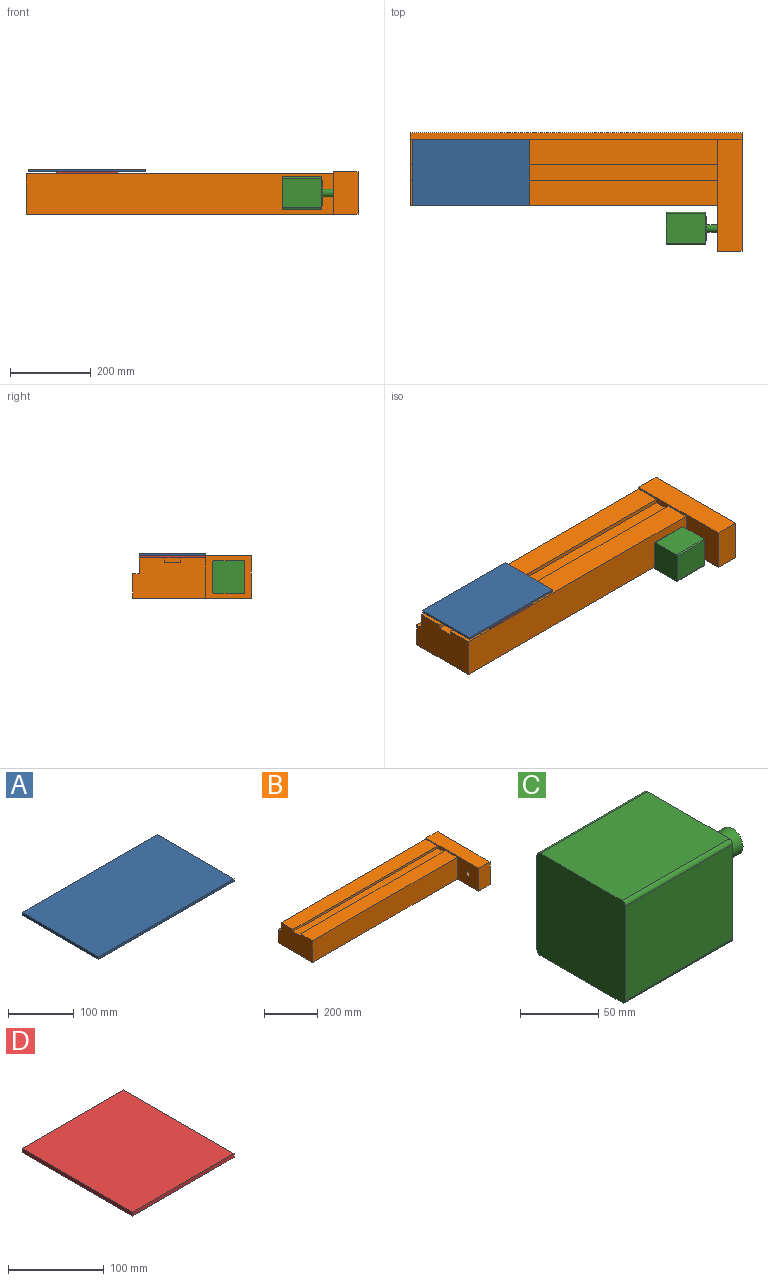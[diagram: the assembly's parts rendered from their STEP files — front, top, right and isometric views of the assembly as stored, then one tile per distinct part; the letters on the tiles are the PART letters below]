
ASSEMBLY  parts=4 mates=3
PART A: 6 faces, bbox 290x165x5 mm
  f0: plane 165x5mm, normal (-1,0,0), area 825mm2, adj f1,f3,f4,f5
  f1: plane 290x5mm, normal (0,-1,0), area 1450mm2, adj f0,f2,f4,f5
  f2: plane 165x5mm, normal (1,0,0), area 825mm2, adj f1,f3,f4,f5
  f3: plane 290x5mm, normal (0,1,0), area 1450mm2, adj f0,f2,f4,f5
  f4: plane 290x165mm, normal (0,0,1), area 47850mm2, adj f0,f1,f2,f3
  f5: plane 290x165mm, normal (0,0,-1), area 47850mm2, adj f0,f1,f2,f3
PART B: 17 faces, bbox 820x293x104 mm
  f0: plane 760x62.5mm, normal (0,0,1), area 47500mm2, adj f1,f6,f10,f12
  f1: plane 181x99mm, normal (-1,0,0), area 16895mm2, adj f0,f2,f3,f4,f5,f6,f11,f12
  f2: plane 760x99mm, normal (0,-1,0), area 75240mm2, adj f1,f3,f10,f11
  f3: plane 820x293mm, normal (0,0,-1), area 155140mm2, adj f1,f2,f4,f8,f9,f10
  f4: plane 820x60mm, normal (0,1,0), area 49200mm2, adj f1,f3,f5,f8
  f5: plane 820x16mm, normal (0,0,1), area 13120mm2, adj f1,f4,f6,f8
  f6: plane 820x44mm, normal (0,1,0), area 32280mm2, adj f0,f1,f5,f7,f8,f10
  f7: plane 277x60mm, normal (0,0,1), area 16620mm2, adj f6,f8,f9,f10
  f8: plane 293x104mm, normal (1,0,0), area 29768mm2, adj f3,f4,f5,f6,f7,f9
  f9: plane 104x60mm, normal (0,-1,0), area 6240mm2, adj f3,f7,f8,f10
  f10: plane 277x104mm, normal (-1,0,0), area 12558.8mm2, adj f0,f2,f3,f6,f7,f9,f11,f12
  f11: plane 760x62.5mm, normal (0,0,1), area 47500mm2, adj f1,f2,f10,f13
  f12: plane 760x10mm, normal (0,-1,0), area 7600mm2, adj f0,f1,f10,f14
  f13: plane 760x10mm, normal (0,1,0), area 7600mm2, adj f1,f10,f11,f14
  f14: plane 760x40mm, normal (0,0,1), area 30400mm2, adj f1,f10,f12,f13
  f15: cylinder r=10mm len=20mm, axis (-1,0,0), area 1256.6mm2, adj f10,f16
  f16: plane 20x20mm, normal (-1,0,0), area 314.2mm2, adj f15
PART C: 14 faces, bbox 137x80x80 mm
  f0: plane 97x74mm, normal (0,0,1), area 7178mm2, adj f4,f5,f10,f13
  f1: plane 97x74mm, normal (0,-1,0), area 7178mm2, adj f4,f5,f10,f11
  f2: plane 97x74mm, normal (0,0,-1), area 7178mm2, adj f4,f5,f11,f12
  f3: plane 97x74mm, normal (0,1,0), area 7178mm2, adj f4,f5,f12,f13
  f4: plane 80x80mm, normal (1,0,0), area 3564.8mm2, adj f0,f1,f2,f3,f6,f10,f11,f12
  f5: plane 80x80mm, normal (-1,0,0), area 6392.3mm2, adj f0,f1,f2,f3,f10,f11,f12,f13
  f6: cylinder r=30mm len=60mm, axis (-1,0,0), area 565.5mm2, adj f4,f7
  f7: plane 60x60mm, normal (1,0,0), area 2543.9mm2, adj f6,f9
  f8: plane 19x19mm, normal (1,0,0), area 283.5mm2, adj f9
  f9: cylinder r=9.5mm len=37mm, axis (-1,0,0), area 2208.5mm2, adj f7,f8
  f10: cylinder r=3mm len=97mm, axis (1,0,0), area 457.1mm2, adj f0,f1,f4,f5
  f11: cylinder r=3mm len=97mm, axis (-1,0,0), area 457.1mm2, adj f1,f2,f4,f5
  f12: cylinder r=3mm len=97mm, axis (1,0,0), area 457.1mm2, adj f2,f3,f4,f5
  f13: cylinder r=3mm len=97mm, axis (-1,0,0), area 457.1mm2, adj f0,f3,f4,f5
PART D: 6 faces, bbox 150x163x5 mm
  f0: plane 163x5mm, normal (1,0,0), area 815mm2, adj f1,f3,f4,f5
  f1: plane 150x5mm, normal (0,1,0), area 750mm2, adj f0,f2,f4,f5
  f2: plane 163x5mm, normal (-1,0,0), area 815mm2, adj f1,f3,f4,f5
  f3: plane 150x5mm, normal (0,-1,0), area 750mm2, adj f0,f2,f4,f5
  f4: plane 163x150mm, normal (0,0,1), area 24450mm2, adj f0,f1,f2,f3
  f5: plane 163x150mm, normal (0,0,-1), area 24450mm2, adj f0,f1,f2,f3
PLACE A t=(-52.31,44.68,87.13)mm
PLACE B rot(axis=(-1,0,0),0deg) t=(-52.31,44.68,87.13)mm fixed
PLACE C rot(axis=(-1,0,0),0deg) t=(-239.31,60.68,75.13)mm
PLACE D t=(-52.31,44.68,87.13)mm
MATE fastened C.f6 <-> B.f15  axis (1,0,0) through (-102.31,-93.82,139.13)mm
MATE slider D.f2 <-> B.f1  axis (-1,0,0) through (-797.31,44.68,186.13)mm
MATE fastened A.f5 <-> D.f4  axis (0,0,-1) through (-722.31,44.68,191.13)mm
